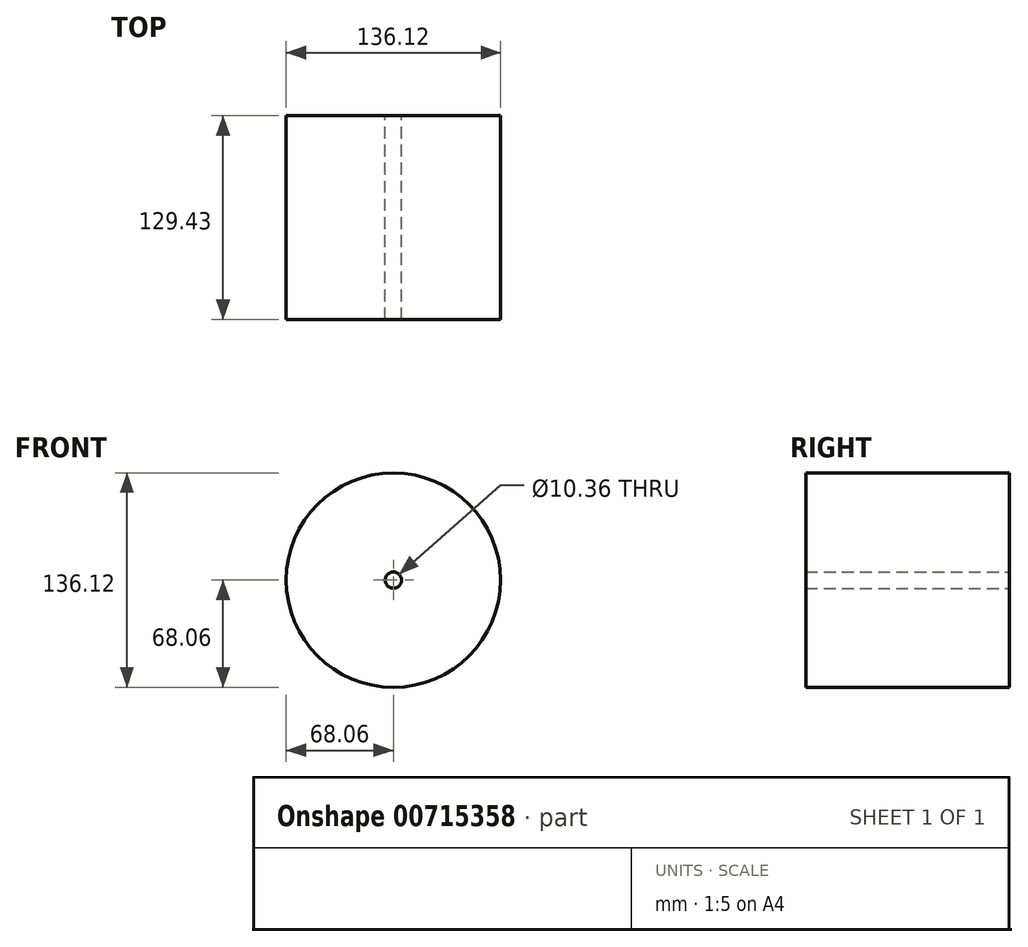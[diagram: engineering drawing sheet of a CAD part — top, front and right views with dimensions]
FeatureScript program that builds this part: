
annotation { "Feature Type Name" : "Feature", "Feature Type Description" : "" }
export const myFeature = defineFeature(function(context is Context, id is Id, definition is map)
    precondition{}
    {
        {
            var Q0;
            Q0=qCreatedBy(makeId("Front.planeOp"),FACE);
            var sketch = newSketch(context, id + "F0", { "sketchPlane" : qUnion([Q0])});
            skCircle(sketch, "E0", {"center": v(0, 0) * mm, "radius": 70.39 * mm});
            skCircle(sketch, "E1", {"center": v(0, 0) * mm, "radius": 68.06 * mm});
            skCircle(sketch, "E2", {"center": v(0, 0) * mm, "radius": 5.18 * mm});
            skSolve(sketch);
        }
        {
            var Q0;
            Q0=makeQuery(id+"F0.imprint","IMPRINT",FACE,{"disambiguationData":[TD([[makeQuery(id+"F0.imprint","IMPRINT",EDGE,{"derivedFrom":sQuery(id+"F0.wireOp",EDGE,"E1")}),1.0]])]});
            extrude(context, id + "F1", {"entities" : qUnion([Q0]), "depth" : 129.43 * mm, "offsetDistance" : 25.4 * mm});
        }
    });
